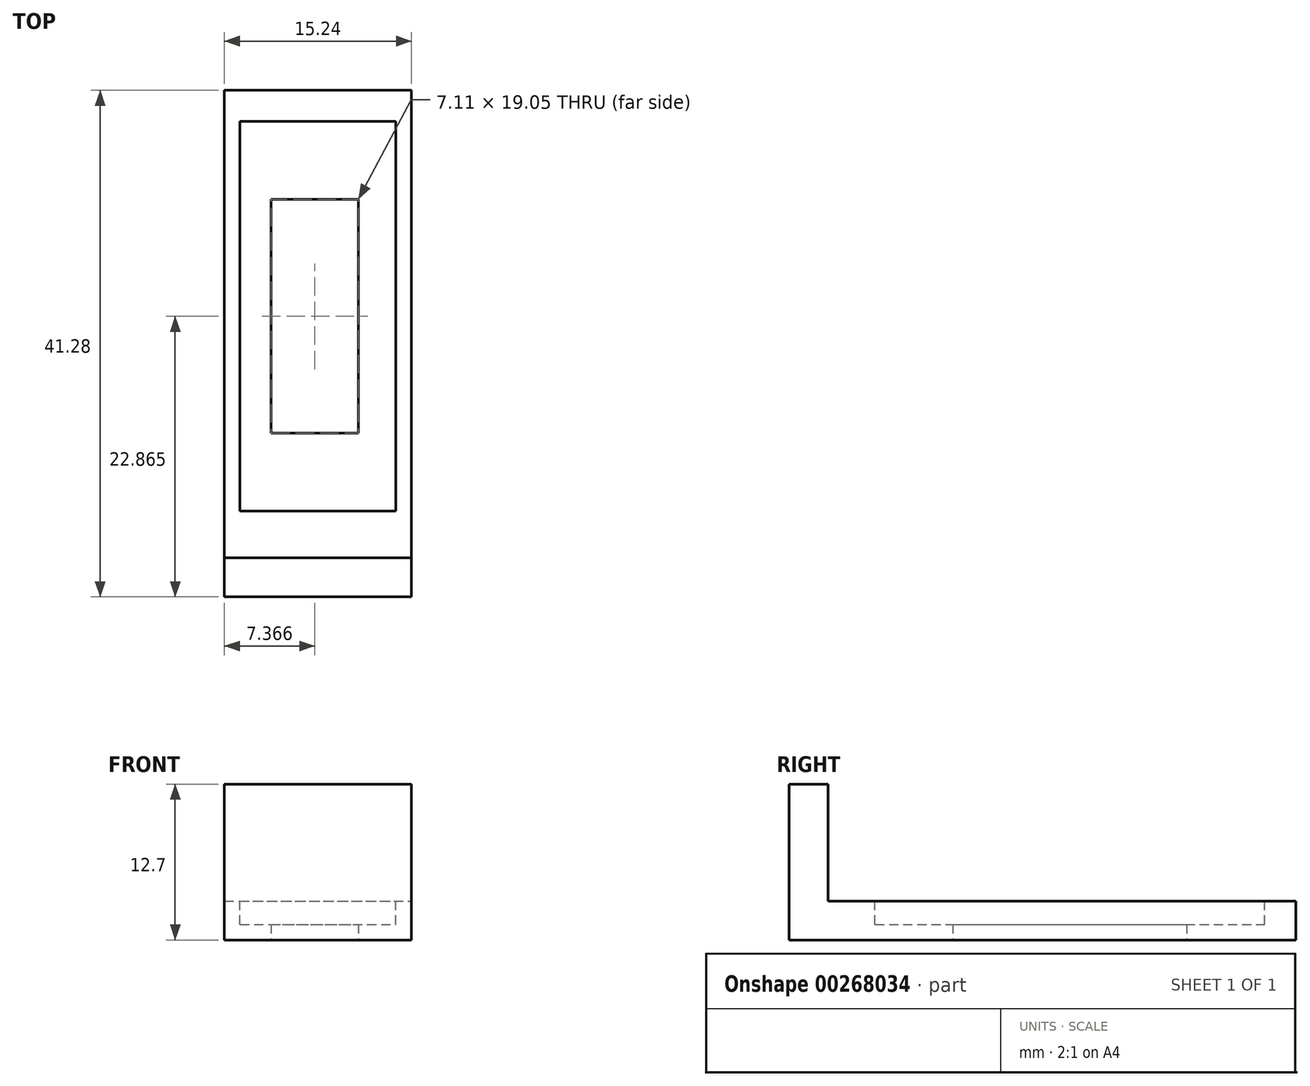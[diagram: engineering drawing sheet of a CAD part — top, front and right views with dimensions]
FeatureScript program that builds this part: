
annotation { "Feature Type Name" : "Feature", "Feature Type Description" : "" }
export const myFeature = defineFeature(function(context is Context, id is Id, definition is map)
    precondition{}
    {
        {
            var Q0;
            Q0=qCreatedBy(makeId("Top.planeOp"),FACE);
            var sketch = newSketch(context, id + "F0", { "sketchPlane" : qUnion([Q0])});
            skLineSegment(sketch, "E0.bottom", {"start": v(0, 0) * mm, "end": v(15.24, 0) * mm});
            skLineSegment(sketch, "E0.top", {"start": v(0, 38.1) * mm, "end": v(15.24, 38.1) * mm});
            skLineSegment(sketch, "E0.left", {"start": v(0, 0) * mm, "end": v(0, 38.1) * mm});
            skLineSegment(sketch, "E0.right", {"start": v(15.24, 0) * mm, "end": v(15.24, 38.1) * mm});
            skLineSegment(sketch, "E1.bottom", {"start": v(3.8, 10.16) * mm, "end": v(10.92, 10.16) * mm});
            skLineSegment(sketch, "E1.top", {"start": v(3.8, 29.21) * mm, "end": v(10.92, 29.21) * mm});
            skLineSegment(sketch, "E1.left", {"start": v(3.8, 10.16) * mm, "end": v(3.8, 29.21) * mm});
            skLineSegment(sketch, "E1.right", {"start": v(10.92, 10.16) * mm, "end": v(10.92, 29.21) * mm});
            skLineSegment(sketch, "E2.bottom", {"start": v(0, 0) * mm, "end": v(3.81, 0) * mm, "construction": true});
            skLineSegment(sketch, "E2.top", {"start": v(0, 10.16) * mm, "end": v(3.8, 10.16) * mm, "construction": true});
            skLineSegment(sketch, "E2.left", {"start": v(0, 0) * mm, "end": v(0, 10.16) * mm, "construction": true});
            skLineSegment(sketch, "E2.right", {"start": v(3.81, 0) * mm, "end": v(3.8, 10.16) * mm, "construction": true});
            skLineSegment(sketch, "E3.top", {"start": v(0, -3.18) * mm, "end": v(15.24, -3.18) * mm});
            skLineSegment(sketch, "E3.left", {"start": v(0, 0) * mm, "end": v(0, -3.18) * mm});
            skLineSegment(sketch, "E3.right", {"start": v(15.24, 0) * mm, "end": v(15.24, -3.18) * mm});
            skSolve(sketch);
        }
        {
            var Q0;
            Q0=makeQuery(id+"F0.imprint","IMPRINT",FACE,{"disambiguationData":[TD([[makeQuery(id+"F0.imprint","IMPRINT",EDGE,{"derivedFrom":sQuery(id+"F0.wireOp",EDGE,"E0.top")}),-1.0]])]});
            extrude(context, id + "F1", {"entities" : qUnion([Q0]), "offsetDistance" : 25.4 * mm, "depth" : 3.17 * mm});
        }
        {
            var Q0;
            Q0=makeQuery(id+"F1.opExtrude","CAP_FACE",FACE,{"disambiguationData":[OSD([sQuery(id+"F0.wireOp",EDGE,"E0.bottom"),sQuery(id+"F0.wireOp",EDGE,"E0.top"),sQuery(id+"F0.wireOp",EDGE,"E0.left"),sQuery(id+"F0.wireOp",EDGE,"E0.right"),sQuery(id+"F0.wireOp",EDGE,"E1.bottom"),sQuery(id+"F0.wireOp",EDGE,"E1.top"),sQuery(id+"F0.wireOp",EDGE,"E1.left"),sQuery(id+"F0.wireOp",EDGE,"E1.right")])],"isStart":false});
            var sketch = newSketch(context, id + "F2", { "sketchPlane" : qUnion([Q0])});
            skLineSegment(sketch, "E4.bottom", {"start": v(1.27, 3.81) * mm, "end": v(13.97, 3.81) * mm});
            skLineSegment(sketch, "E4.top", {"start": v(1.27, 35.56) * mm, "end": v(13.97, 35.56) * mm});
            skLineSegment(sketch, "E4.left", {"start": v(1.27, 3.81) * mm, "end": v(1.27, 35.56) * mm});
            skLineSegment(sketch, "E4.right", {"start": v(13.97, 3.81) * mm, "end": v(13.97, 35.56) * mm});
            skLineSegment(sketch, "E5.bottom", {"start": v(3.8, 10.16) * mm, "end": v(1.27, 10.16) * mm, "construction": true});
            skLineSegment(sketch, "E5.top", {"start": v(3.81, 3.81) * mm, "end": v(1.27, 3.81) * mm, "construction": true});
            skLineSegment(sketch, "E5.left", {"start": v(3.8, 10.16) * mm, "end": v(3.81, 3.81) * mm, "construction": true});
            skLineSegment(sketch, "E5.right", {"start": v(1.27, 10.16) * mm, "end": v(1.27, 3.81) * mm, "construction": true});
            skSolve(sketch);
        }
        {
            var Q0;
            Q0=makeQuery(id+"F2.imprint","IMPRINT",FACE,{"disambiguationData":[TD([[makeQuery(id+"F2.imprint","IMPRINT",EDGE,{"derivedFrom":sQuery(id+"F2.wireOp",EDGE,"E4.bottom")}),1.0]])]});
            extrude(context, id + "F3", {"entities" : qUnion([Q0]), "operationType" : NewBodyOperationType.REMOVE, "oppositeDirection" : true, "offsetDistance" : 25.4 * mm, "depth" : 1.9 * mm});
        }
        {
            var Q0;
            Q0=makeQuery(id+"F0.imprint","IMPRINT",FACE,{"disambiguationData":[TD([[makeQuery(id+"F0.imprint","IMPRINT",EDGE,{"derivedFrom":sQuery(id+"F0.wireOp",EDGE,"E0.bottom")}),-1.0]])]});
            extrude(context, id + "F4", {"entities" : qUnion([Q0]), "operationType" : NewBodyOperationType.ADD, "depth" : 12.7 * mm});
        }
    });
